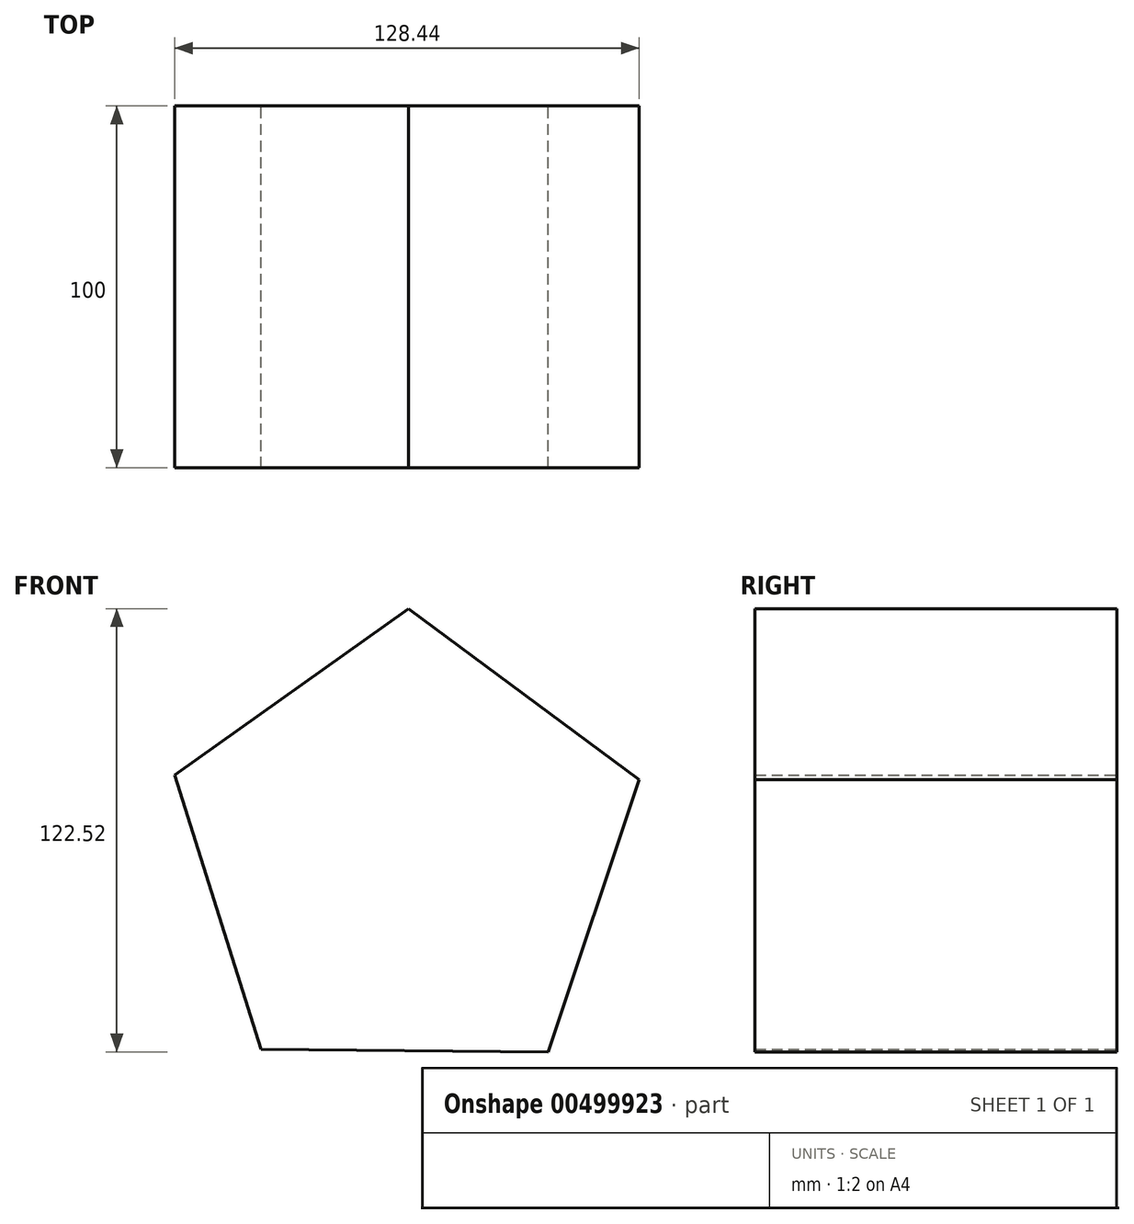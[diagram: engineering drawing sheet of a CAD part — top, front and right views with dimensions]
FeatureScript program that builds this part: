
annotation { "Feature Type Name" : "Feature", "Feature Type Description" : "" }
export const myFeature = defineFeature(function(context is Context, id is Id, definition is map)
    precondition{}
    {
        {
            var Q0;
            Q0=qCreatedBy(makeId("Front.planeOp"),FACE);
            var sketch = newSketch(context, id + "F0", { "sketchPlane" : qUnion([Q0])});
            skCircle(sketch, "E0.cCircle", {"center": v(0, 0) * mm, "radius": 67.53 * mm, "construction": true});
            skLineSegment(sketch, "E0.0", {"start": v(64.42, 20.26) * mm, "end": v(39.17, -55) * mm});
            skLineSegment(sketch, "E0.1", {"start": v(39.17, -55) * mm, "end": v(-40.2, -54.25) * mm});
            skLineSegment(sketch, "E0.2", {"start": v(-40.2, -54.25) * mm, "end": v(-64.02, 21.47) * mm});
            skLineSegment(sketch, "E0.3", {"start": v(-64.02, 21.47) * mm, "end": v(0.64, 67.52) * mm});
            skLineSegment(sketch, "E0.4", {"start": v(0.64, 67.52) * mm, "end": v(64.42, 20.26) * mm});
            skSolve(sketch);
        }
        {
            var Q0;
            Q0=makeQuery(id+"F0.imprint","IMPRINT",FACE,{"disambiguationData":[TD([[makeQuery(id+"F0.imprint","IMPRINT",EDGE,{"derivedFrom":sQuery(id+"F0.wireOp",EDGE,"E0.0")}),-1.0]])]});
            extrude(context, id + "F1", {"entities" : qUnion([Q0]), "depth" : 100 * mm, "symmetric" : true});
        }
    });
